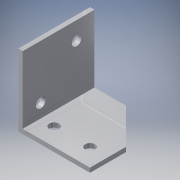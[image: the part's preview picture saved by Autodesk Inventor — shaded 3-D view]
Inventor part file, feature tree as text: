
AUTODESK INVENTOR PART (.ipt)
format: ipt  version: 2016 (Build 200138000, 138)  size: 125,952 bytes
history: native  units: in
note: dims shown in document units (in); Inventor stores cm internally (conversion verified against a paired STEP export)
features: extrude x3, sketch x3
ambient origin geometry x8: Origin, YZ Plane, XZ Plane, XY Plane, X Axis, Y Axis, Z Axis, Center Point
bodies: Solid1 (feature_tree)
feature tree (6):
  extrude  "Extrusion1"  Depth=0.125in
  sketch  "Sketch2"  dims[d2=1.875in d3=1.875in]
  extrude  "Extrusion3"  Depth=1.875in
  extrude  "Extrusion4"  Depth=0.125in
  sketch  "Sketch1"  dims[d0=2.0in d1=0.125in]
  sketch  "Sketch3"  dims[d4=2.0in d5=0.0in d6=0.875in d7=0.2656in d8=0.2656in d9=0.5in d10=0.5in d11=1.5in d12=1.5in d15=0.2656in d16=0.2656in d17=0.5in d18=0.5in d19=0.5in d20=0.5in d21=0.125in d22=0.0in d23=0.125in d24=0.0in]
